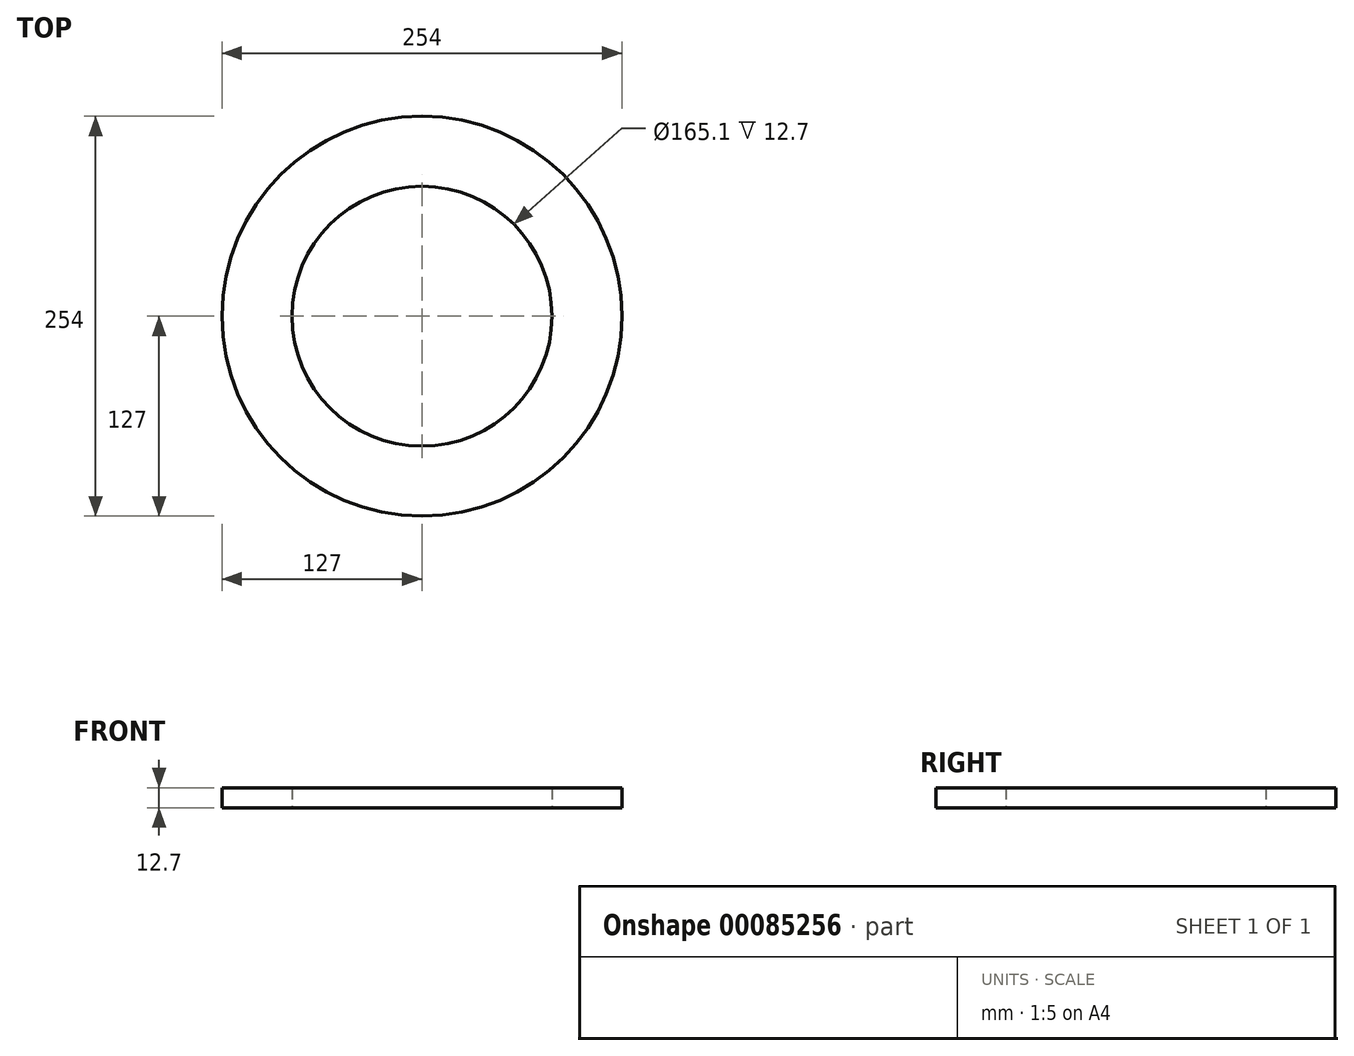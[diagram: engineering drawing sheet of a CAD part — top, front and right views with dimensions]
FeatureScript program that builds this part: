
annotation { "Feature Type Name" : "Feature", "Feature Type Description" : "" }
export const myFeature = defineFeature(function(context is Context, id is Id, definition is map)
    precondition{}
    {
        {
            var Q0;
            Q0=qCreatedBy(makeId("Top.planeOp"),FACE);
            var sketch = newSketch(context, id + "F0", { "sketchPlane" : qUnion([Q0])});
            skCircle(sketch, "E0", {"center": v(0, 0) * mm, "radius": 127 * mm});
            skCircle(sketch, "E1", {"center": v(0, 0) * mm, "radius": 82.55 * mm});
            skSolve(sketch);
        }
        {
            var Q0;
            Q0=makeQuery(id+"F0.imprint","IMPRINT",FACE,{"disambiguationData":[TD([[makeQuery(id+"F0.imprint","IMPRINT",EDGE,{"derivedFrom":sQuery(id+"F0.wireOp",EDGE,"E0")}),1.0]])]});
            extrude(context, id + "F1", {"entities" : qUnion([Q0]), "depth" : 12.7 * mm});
        }
    });
